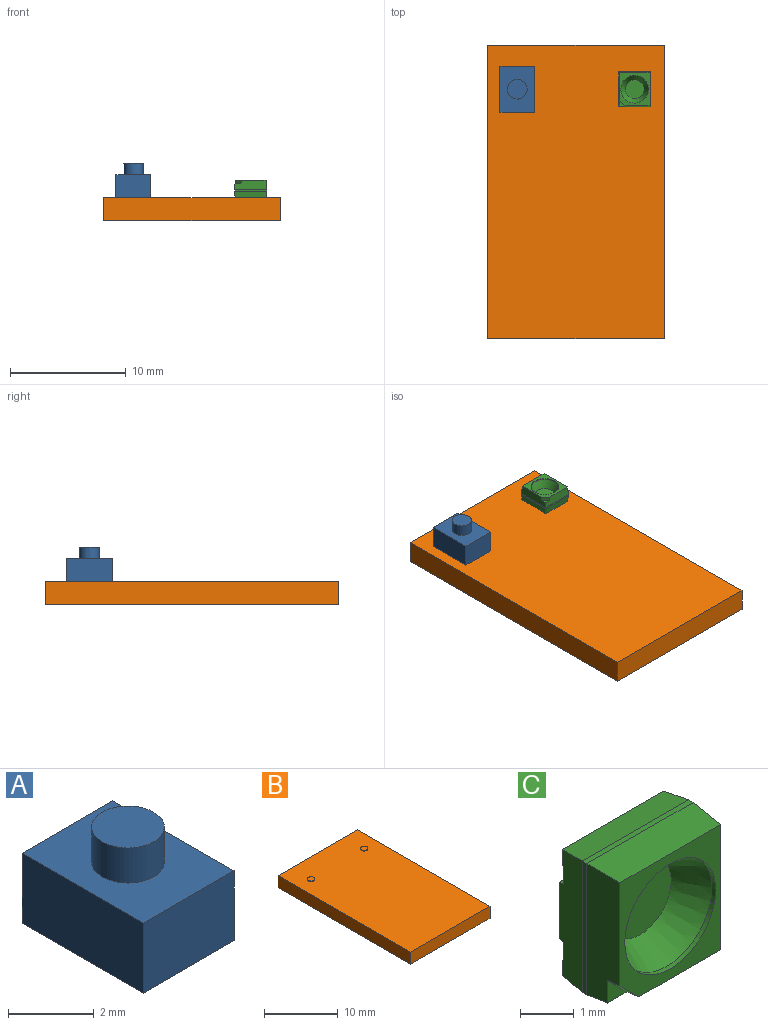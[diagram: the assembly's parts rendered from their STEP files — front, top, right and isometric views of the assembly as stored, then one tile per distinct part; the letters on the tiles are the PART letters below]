
ASSEMBLY  parts=3 mates=2
PART A: 8 faces, bbox 3x4x3 mm
  f0: plane 4x2mm, normal (-1,0,0), area 8mm2, adj f1,f3,f4,f5
  f1: plane 3x2mm, normal (0,-1,0), area 6mm2, adj f0,f2,f4,f5
  f2: plane 4x2mm, normal (1,0,0), area 8mm2, adj f1,f3,f4,f5
  f3: plane 3x2mm, normal (0,1,0), area 6mm2, adj f0,f2,f4,f5
  f4: plane 4x3mm, normal (0,0,1), area 9.7mm2, adj f0,f1,f2,f3,f6
  f5: plane 4x3mm, normal (0,0,-1), area 12mm2, adj f0,f1,f2,f3
  f6: cylinder r=0.85mm len=1.7mm, axis (0,0,-1), area 5.3mm2, adj f4,f7
  f7: plane 1.7x1.7mm, normal (0,0,1), area 2.3mm2, adj f6
PART B: 10 faces, bbox 15.2x25.4x2.1 mm
  f0: plane 25.4x2mm, normal (1,0,0), area 50.8mm2, adj f1,f3,f4,f5
  f1: plane 15.24x2mm, normal (0,1,0), area 30.5mm2, adj f0,f2,f4,f5
  f2: plane 25.4x2mm, normal (-1,0,0), area 50.8mm2, adj f1,f3,f4,f5
  f3: plane 15.24x2mm, normal (0,-1,0), area 30.5mm2, adj f0,f2,f4,f5
  f4: plane 25.4x15.24mm, normal (0,0,1), area 385.5mm2, adj f0,f1,f2,f3,f6,f8
  f5: plane 25.4x15.24mm, normal (0,0,-1), area 387.1mm2, adj f0,f1,f2,f3
  f6: cylinder r=0.5mm len=1mm, axis (0,0,-1), area 0.3mm2, adj f4,f7
  f7: plane 1x1mm, normal (0,0,1), area 0.8mm2, adj f6
  f8: cylinder r=0.5mm len=1mm, axis (0,0,-1), area 0.3mm2, adj f4,f9
  f9: plane 1x1mm, normal (0,0,1), area 0.8mm2, adj f8
PART C: 25 faces, bbox 2.8x1.6x3 mm
  f0: cylinder r=1.2mm len=2.4mm, axis (0,1,0), area 0.8mm2, adj f1,f16
  f1: cone r=1.01mm half-angle=28.2deg, axis (0,-1,0), area 5.1mm2, adj f0,f11
  f2: cylinder r=0.5mm len=1mm, axis (0,-1,0), area 0.6mm2, adj f3,f6
  f3: plane 1x1mm, normal (0,1,0), area 0.8mm2, adj f2
  f4: plane 2.69x0.13mm, normal (0,0.1,-0.99), area 0.3mm2, adj f5,f6,f8,f21
  f5: plane 3x0.68mm, normal (0.99,0.1,0), area 1.8mm2, adj f4,f6,f7,f8,f9,f10,f22,f23
  f6: plane 2.66x1.29mm, normal (0,1,0), area 2.7mm2, adj f2,f4,f5,f7,f21
  f7: plane 2.69x0.13mm, normal (0,0.1,0.99), area 0.3mm2, adj f5,f6,f9,f21
  f8: plane 2.69x0.78mm, normal (0,1,0.05), area 2.1mm2, adj f4,f5,f10,f21
  f9: plane 2.69x0.78mm, normal (0,1,-0.05), area 2.1mm2, adj f5,f7,f21,f23
  f10: plane 2.8x0.59mm, normal (0,0.1,-0.99), area 1.6mm2, adj f5,f8,f19,f21
  f11: plane 1.65x1.65mm, normal (0,-1,0), area 2.1mm2, adj f1
  f12: plane 0.52x0.52mm, normal (0,-1,0), area 0.1mm2, adj f13,f14,f18
  f13: plane 0.53x0.53mm, normal (-0.7,-0.09,-0.7), area 0.2mm2, adj f12,f14,f16,f18
  f14: plane 3x0.8mm, normal (-1,-0.09,0), area 2.2mm2, adj f12,f13,f16,f17,f18,f20
  f15: plane 3x0.8mm, normal (1,-0.09,0), area 2.4mm2, adj f16,f17,f18,f22
  f16: plane 2.86x2.66mm, normal (0,-1,0), area 3mm2, adj f0,f13,f14,f15,f17,f18
  f17: plane 2.8x0.8mm, normal (0,-0.09,1), area 2.2mm2, adj f14,f15,f16,f24
  f18: plane 2.8x0.8mm, normal (0,-0.09,-1), area 2mm2, adj f12,f13,f14,f15,f16,f19
  f19: plane 2.8x0.13mm, normal (0,0,-1), area 0.3mm2, adj f10,f18,f20,f22
  f20: plane 3x0.13mm, normal (-1,0,0), area 0.4mm2, adj f14,f19,f21,f24
  f21: plane 3x0.68mm, normal (-0.99,0.1,0), area 1.8mm2, adj f4,f6,f7,f8,f9,f10,f20,f23
  f22: plane 3x0.13mm, normal (1,0,0), area 0.4mm2, adj f5,f15,f19,f24
  f23: plane 2.8x0.59mm, normal (0,0.1,0.99), area 1.6mm2, adj f5,f9,f21,f24
  f24: plane 2.8x0.13mm, normal (0,0,1), area 0.4mm2, adj f17,f20,f22,f23
PLACE A t=(-14.2,23.59,2)mm
PLACE B t=(-7.62,12.7,0)mm
PLACE C rot(axis=(-1,0,0),90deg) t=(-2.54,21.59,2.3)mm
MATE fastened A.f6 <-> B.f8  axis (0,0,-1) through (-12.7,21.59,2)mm
MATE fastened B.f6 <-> C.f1  axis (0,0,1) through (-2.54,21.59,2.1)mm
